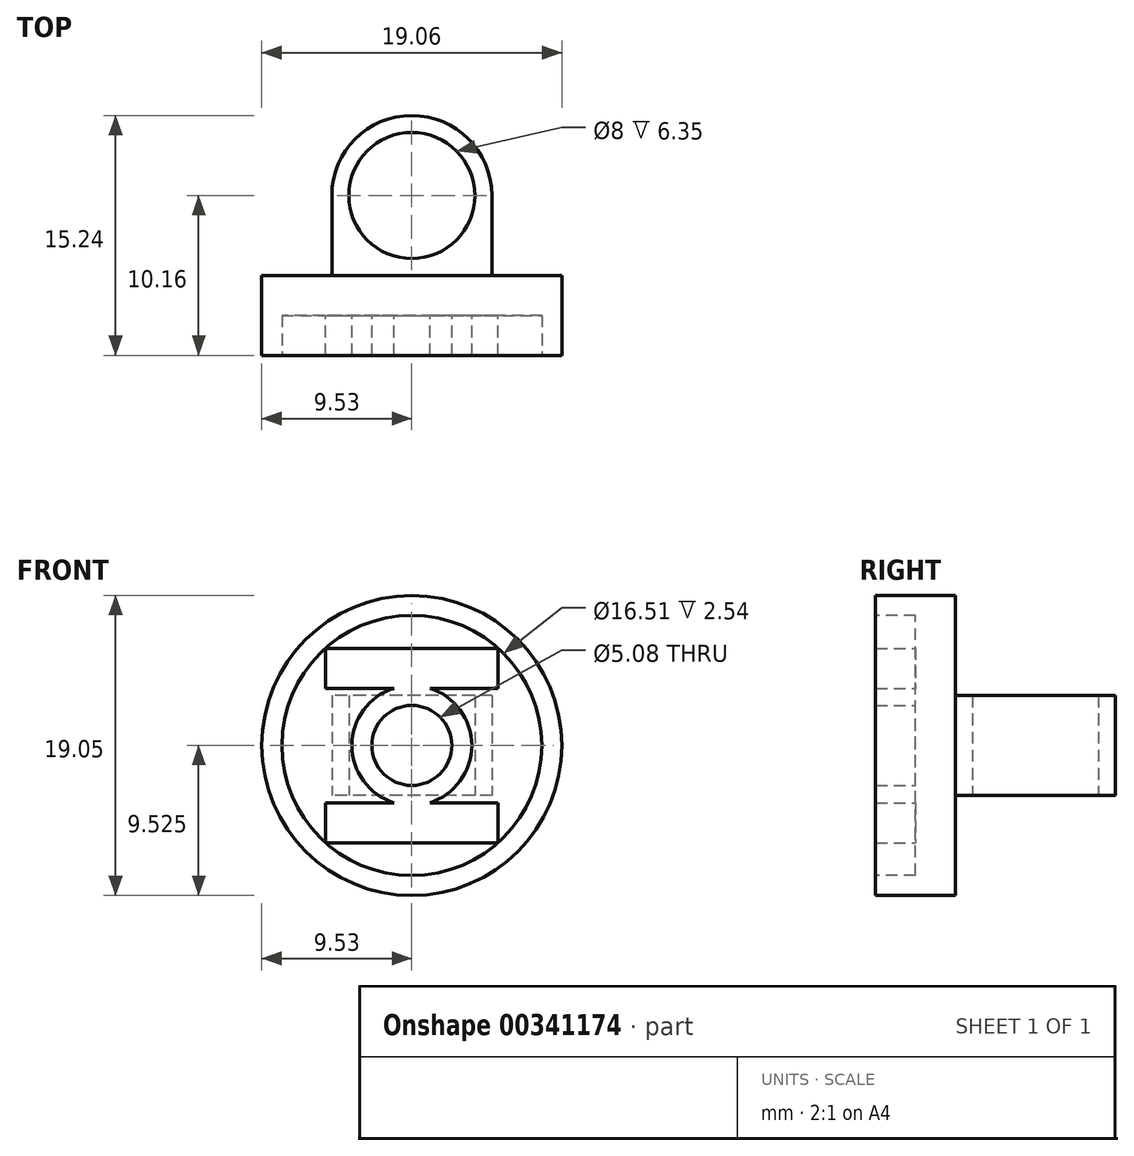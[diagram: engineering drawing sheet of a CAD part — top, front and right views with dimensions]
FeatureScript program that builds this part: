
annotation { "Feature Type Name" : "Feature", "Feature Type Description" : "" }
export const myFeature = defineFeature(function(context is Context, id is Id, definition is map)
    precondition{}
    {
        {
            var Q0;
            Q0=qCreatedBy(makeId("Top.planeOp"),FACE);
            var sketch = newSketch(context, id + "F0", { "sketchPlane" : qUnion([Q0])});
            skCircle(sketch, "E0", {"center": v(0, 0) * mm, "radius": 4 * mm});
            skLineSegment(sketch, "E1.bottom", {"start": v(5.08, 5.08) * mm, "end": v(-5.08, 5.08) * mm});
            skLineSegment(sketch, "E1.top", {"start": v(5.08, -5.08) * mm, "end": v(-5.08, -5.08) * mm});
            skLineSegment(sketch, "E1.left", {"start": v(5.08, 5.08) * mm, "end": v(5.08, -5.08) * mm});
            skLineSegment(sketch, "E1.right", {"start": v(-5.08, 5.08) * mm, "end": v(-5.08, -5.08) * mm});
            skSolve(sketch);
        }
        {
            var Q0;
            Q0=makeQuery(id+"F0.imprint","IMPRINT",FACE,{"disambiguationData":[TD([[makeQuery(id+"F0.imprint","IMPRINT",EDGE,{"derivedFrom":sQuery(id+"F0.wireOp",EDGE,"E0")}),-1.0]])]});
            extrude(context, id + "F1", {"entities" : qUnion([Q0]), "depth" : 6.35 * mm});
        }
        {
            var Q0;
            Q0=makeQuery(id+"F1.opExtrude","SWEPT_FACE",FACE,{"disambiguationData":[OSD([sQuery(id+"F0.wireOp",EDGE,"E1.top")])]});
            var sketch = newSketch(context, id + "F2", { "sketchPlane" : qUnion([Q0])});
            skCircle(sketch, "E2", {"center": v(0, 3.18) * mm, "radius": 9.53 * mm});
            skPoint(sketch, "E2.centerSnap0", {"position": v(5.08, 3.18) * mm});
            skSolve(sketch);
        }
        {
            var Q0;
            Q0 = qSketchRegion(id + "F2", true);
            extrude(context, id + "F3", {"entities" : qUnion([Q0]), "operationType" : NewBodyOperationType.ADD, "depth" : 5.08 * mm});
        }
        {
            var Q0;
            Q0=makeQuery(id+"F1.opExtrude","SWEPT_EDGE",EDGE,{"disambiguationData":[OSD([sQuery(id+"F0.wireOp",EDGE,"E1.top"),sQuery(id+"F0.wireOp",EDGE,"E1.left")])]});
            var Q1;
            Q1=makeQuery(id+"F1.opExtrude","CAP_EDGE",EDGE,{"disambiguationData":[OSD([sQuery(id+"F0.wireOp",EDGE,"E1.top")])],"isStart":true});
            var Q2;
            Q2=makeQuery(id+"F1.opExtrude","SWEPT_EDGE",EDGE,{"disambiguationData":[OSD([sQuery(id+"F0.wireOp",EDGE,"E1.top"),sQuery(id+"F0.wireOp",EDGE,"E1.right")])]});
            var Q3;
            Q3=makeQuery(id+"F1.opExtrude","CAP_EDGE",EDGE,{"disambiguationData":[OSD([sQuery(id+"F0.wireOp",EDGE,"E1.top")])],"isStart":false});
            var Q4;
            Q4=makeQuery(id+"F1.opExtrude","SWEPT_EDGE",EDGE,{"disambiguationData":[OSD([sQuery(id+"F0.wireOp",EDGE,"E1.bottom"),sQuery(id+"F0.wireOp",EDGE,"E1.right")])]});
            var Q5;
            Q5=makeQuery(id+"F1.opExtrude","SWEPT_EDGE",EDGE,{"disambiguationData":[OSD([sQuery(id+"F0.wireOp",EDGE,"E1.bottom"),sQuery(id+"F0.wireOp",EDGE,"E1.left")])]});
            fillet(context, id + "F4", {"entities" : qUnion([Q0, Q1, Q2, Q3, Q4, Q5]), "radius" : 5.08 * mm, "tangentPropagation" : true, "allowEdgeOverflow" : false});
        }
        {
            var Q0;
            Q0=makeQuery(id+"F3.opExtrude","CAP_FACE",FACE,{"disambiguationData":[OSD([sQuery(id+"F2.wireOp",EDGE,"E2")])],"isStart":false});
            var sketch = newSketch(context, id + "F5", { "sketchPlane" : qUnion([Q0])});
            skCircle(sketch, "E3", {"center": v(0, 3.18) * mm, "radius": 8.26 * mm});
            skSolve(sketch);
        }
        {
            var Q0;
            Q0=makeQuery(id+"F5.imprint","IMPRINT",FACE,{"disambiguationData":[TD([[makeQuery(id+"F5.imprint","IMPRINT",EDGE,{"derivedFrom":sQuery(id+"F5.wireOp",EDGE,"E3")}),1.0]])]});
            extrude(context, id + "F6", {"entities" : qUnion([Q0]), "operationType" : NewBodyOperationType.REMOVE, "oppositeDirection" : true, "depth" : 2.54 * mm});
        }
        {
            var Q0;
            Q0=makeQuery(id+"F6.boolean.opBoolean","COPY",FACE,{"derivedFrom":makeQuery(id+"F6.opExtrude","CAP_FACE",FACE,{"disambiguationData":[OSD([sQuery(id+"F5.wireOp",EDGE,"E3")])],"isStart":false})});
            var sketch = newSketch(context, id + "F7", { "sketchPlane" : qUnion([Q0])});
            skArc(sketch, "E4", {"start": v(-1.14, 6.8) * mm, "mid": v(-3.81, 3.18) * mm, "end": v(-1.14, -0.46) * mm});
            skCircle(sketch, "E5", {"center": v(0, 3.18) * mm, "radius": 2.54 * mm});
            skLineSegment(sketch, "E6.top", {"start": v(-1.14, 6.8) * mm, "end": v(-5.48, 6.8) * mm});
            skLineSegment(sketch, "E6.left", {"start": v(0, 6.8) * mm, "end": v(0, 6.99) * mm});
            skLineSegment(sketch, "E6.right", {"start": v(-5.48, 6.8) * mm, "end": v(-5.48, 6.99) * mm});
            skLineSegment(sketch, "E7", {"start": v(-5.48, 6.8) * mm, "end": v(-5.48, 9.35) * mm});
            skLineSegment(sketch, "E8", {"start": v(-5.48, 9.35) * mm, "end": v(5.48, 9.35) * mm});
            skLineSegment(sketch, "E9", {"start": v(5.48, 9.35) * mm, "end": v(5.48, 6.8) * mm});
            skLineSegment(sketch, "E10", {"start": v(5.48, 6.8) * mm, "end": v(1.14, 6.8) * mm});
            skLineSegment(sketch, "E11", {"start": v(0, 3.18) * mm, "end": v(4.82, 3.18) * mm, "construction": true});
            skLineSegment(sketch, "E12.MirrorCS", {"start": v(5.48, -0.46) * mm, "end": v(1.14, -0.46) * mm});
            skLineSegment(sketch, "E13.MirrorCS", {"start": v(-1.14, -0.46) * mm, "end": v(-5.48, -0.46) * mm});
            skLineSegment(sketch, "E14.MirrorCS", {"start": v(5.48, -3) * mm, "end": v(5.48, -0.46) * mm});
            skLineSegment(sketch, "E15.MirrorCS", {"start": v(-5.48, -3) * mm, "end": v(5.48, -3) * mm});
            skLineSegment(sketch, "E16.MirrorCS", {"start": v(-5.48, -0.46) * mm, "end": v(-5.48, -3) * mm});
            skPoint(sketch, "E17.orphan", {"position": v(0, -0.46) * mm});
            skArc(sketch, "E18.trimOffspring", {"start": v(1.14, -0.46) * mm, "mid": v(3.81, 3.18) * mm, "end": v(1.14, 6.8) * mm});
            skSolve(sketch);
        }
        {
            var Q0;
            Q0=makeQuery(id+"F7.imprint","IMPRINT",FACE,{"disambiguationData":[TD([[makeQuery(id+"F7.imprint","IMPRINT",EDGE,{"derivedFrom":sQuery(id+"F7.wireOp",EDGE,"E4")}),1.0]])]});
            var Q1;
            Q1=makeQuery(id+"F3.opExtrude","CAP_FACE",FACE,{"disambiguationData":[OSD([sQuery(id+"F2.wireOp",EDGE,"E2")])],"isStart":false});
            extrude(context, id + "F8", {"entities" : qUnion([Q0]), "endBound" : BoundingType.UP_TO_SURFACE, "endBoundEntityFace" : qUnion([Q1]), "depth" : 25.4 * mm});
        }
    });
